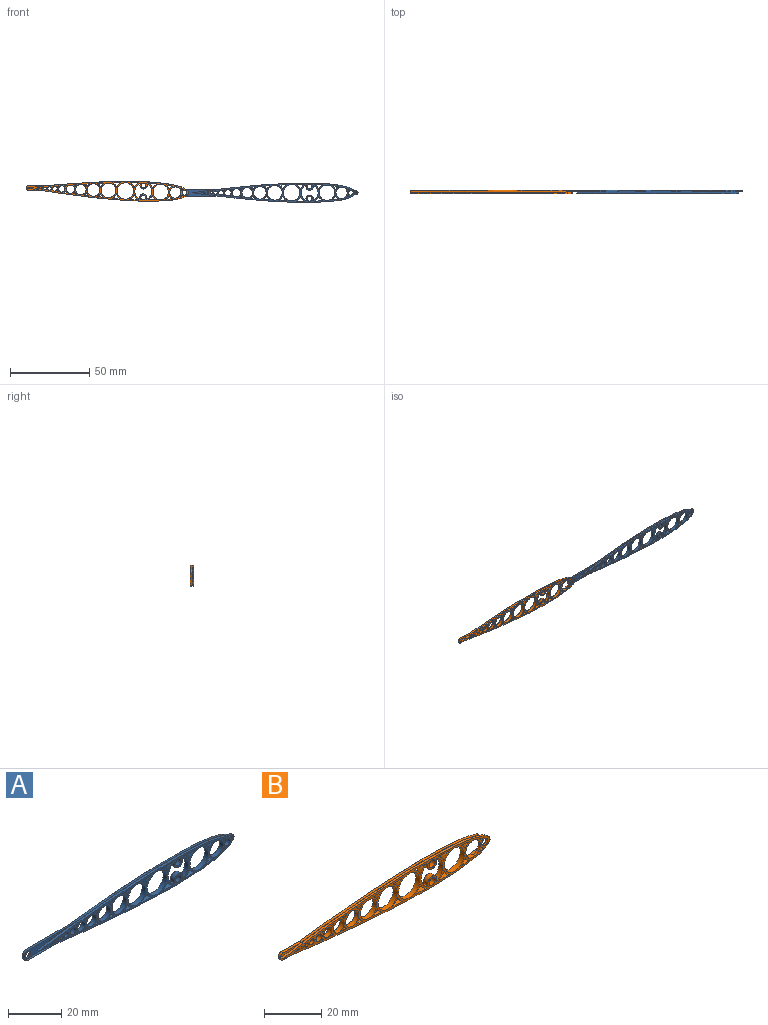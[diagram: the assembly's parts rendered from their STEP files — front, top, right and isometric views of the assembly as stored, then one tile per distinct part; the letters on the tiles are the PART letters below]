
ASSEMBLY  parts=2 mates=1
PART A: 123 faces, bbox 111.8x2x12.5 mm
  f0: extruded ~2.08x1.05mm, area 2.2mm2, adj f1,f111,f112,f114
  f1: extruded ~9.57x1.31mm, area 10.1mm2, adj f0,f2,f112,f114
  f2: extruded ~9.57x1.31mm, area 10.1mm2, adj f1,f3,f112,f114
  f3: extruded ~2.08x1.05mm, area 2.2mm2, adj f2,f4,f112,f114
  f4: extruded ~2.68x1.05mm, area 2.8mm2, adj f3,f5,f112,f114
  f5: extruded ~3.42x1.05mm, area 3.6mm2, adj f4,f6,f112,f114
  f6: extruded ~4.32x1.05mm, area 4.6mm2, adj f5,f7,f112,f114
  f7: extruded ~5.4x1.05mm, area 5.7mm2, adj f6,f8,f112,f114
  f8: extruded ~6.65x1.05mm, area 7mm2, adj f7,f9,f112,f114
  f9: extruded ~8.03x1.05mm, area 8.5mm2, adj f8,f10,f112,f114
  f10: extruded ~9.47x1.05mm, area 10mm2, adj f9,f11,f112,f114
  f11: extruded ~10.77x1.05mm, area 11.3mm2, adj f10,f12,f112,f114
  f12: extruded ~11.59x1.05mm, area 12.2mm2, adj f11,f13,f112,f114
  f13: extruded ~11.42x1.05mm, area 12mm2, adj f12,f14,f112,f114
  f14: extruded ~9.7x1.4mm, area 10.3mm2, adj f13,f15,f112,f114
  f15: extruded ~6.29x2.42mm, area 7.1mm2, adj f14,f16,f112,f114
  f16: extruded ~1.82x1.12mm, area 2.3mm2, adj f15,f17,f112,f114
  f17: extruded ~1.82x1.12mm, area 2.3mm2, adj f16,f18,f112,f114
  f18: extruded ~6.29x2.42mm, area 7.1mm2, adj f17,f19,f112,f114
  f19: extruded ~9.7x1.4mm, area 10.3mm2, adj f18,f20,f112,f114
  f20: extruded ~11.42x1.05mm, area 12mm2, adj f19,f21,f112,f114
  f21: extruded ~11.59x1.05mm, area 12.2mm2, adj f20,f22,f112,f114
  f22: extruded ~10.77x1.05mm, area 11.3mm2, adj f21,f23,f112,f114
  f23: extruded ~9.47x1.05mm, area 10mm2, adj f22,f24,f112,f114
  f24: extruded ~8.03x1.05mm, area 8.5mm2, adj f23,f25,f112,f114
  f25: extruded ~6.65x1.05mm, area 7mm2, adj f24,f26,f112,f114
  f26: extruded ~5.4x1.05mm, area 5.7mm2, adj f25,f27,f112,f114
  f27: extruded ~4.32x1.05mm, area 4.6mm2, adj f26,f28,f112,f114
  f28: extruded ~3.42x1.05mm, area 3.6mm2, adj f27,f111,f112,f114
  f29: extruded ~2x1.69mm, area 3.6mm2, adj f30,f75,f112,f113
  f30: cylinder r=4.35mm len=2mm, axis (0,1,0), area 3mm2, adj f29,f75,f112,f113
  f31: extruded ~2x1.69mm, area 3.6mm2, adj f32,f76,f112,f113
  f32: cylinder r=2.3mm len=2mm, axis (0,1,0), area 2.4mm2, adj f31,f76,f112,f113
  f33: extruded ~4.07x2mm, area 8.2mm2, adj f34,f77,f112,f113
  f34: cylinder r=4.35mm len=2.12mm, axis (0,1,0), area 6mm2, adj f33,f77,f112,f113
  f35: extruded ~4.07x2mm, area 8.2mm2, adj f36,f79,f112,f113
  f36: cylinder r=5.66mm len=2.61mm, axis (0,1,0), area 6.6mm2, adj f35,f79,f112,f113
  f37: extruded ~4.88x2mm, area 9.8mm2, adj f38,f80,f112,f113
  f38: cylinder r=5.98mm len=2.96mm, axis (0,1,0), area 7.8mm2, adj f37,f80,f112,f113
  f39: extruded ~4.88x2mm, area 9.8mm2, adj f40,f81,f112,f113
  f40: cylinder r=5.45mm len=2.72mm, axis (0,1,0), area 7.5mm2, adj f39,f81,f112,f113
  f41: extruded ~3.96x2mm, area 7.9mm2, adj f42,f82,f112,f113
  f42: cylinder r=5.45mm len=2.48mm, axis (0,1,0), area 6.4mm2, adj f41,f82,f112,f113
  f43: extruded ~3.96x2mm, area 7.9mm2, adj f44,f84,f112,f113
  f44: cylinder r=4.77mm len=2.19mm, axis (0,1,0), area 6.1mm2, adj f43,f84,f112,f113
  f45: extruded ~2.96x2mm, area 5.9mm2, adj f46,f86,f112,f113
  f46: cylinder r=4.07mm len=2mm, axis (0,1,0), area 4.5mm2, adj f45,f86,f112,f113
  f47: extruded ~2.96x2mm, area 5.9mm2, adj f48,f87,f112,f113
  f48: cylinder r=4.77mm len=2mm, axis (0,1,0), area 4.8mm2, adj f47,f87,f112,f113
  f49: extruded ~2.04x2mm, area 4.1mm2, adj f50,f88,f112,f113
  f50: cylinder r=4.07mm len=2mm, axis (0,1,0), area 3.4mm2, adj f49,f88,f112,f113
  f51: extruded ~2.04x2mm, area 4.1mm2, adj f52,f90,f112,f113
  f52: cylinder r=3.41mm len=2mm, axis (0,1,0), area 3.1mm2, adj f51,f90,f112,f113
  f53: extruded ~2x1.25mm, area 2.5mm2, adj f54,f92,f112,f113
  f54: cylinder r=2.83mm len=2mm, axis (0,1,0), area 1.9mm2, adj f53,f92,f112,f113
  f55: extruded ~2x1.25mm, area 2.5mm2, adj f56,f93,f112,f113
  f56: cylinder r=3.41mm len=2mm, axis (0,1,0), area 2.1mm2, adj f55,f93,f112,f113
  f57: cylinder r=5.34mm len=9.93mm, axis (0,1,0), area 25.5mm2, adj f58,f95,f112,f113
  f58: cylinder r=2.3mm len=4.6mm, axis (0,1,0), area 19.1mm2, adj f57,f59,f112,f113
  f59: cylinder r=5.34mm len=9.85mm, axis (0,1,0), area 25.1mm2, adj f58,f95,f112,f113
  f60: extruded ~5.47x2mm, area 10.9mm2, adj f61,f96,f112,f113
  f61: cylinder r=6.14mm len=3.18mm, axis (0,1,0), area 8.6mm2, adj f60,f96,f112,f113
  f62: extruded ~5.33x2mm, area 10.7mm2, adj f63,f98,f112,f113
  f63: cylinder r=5.66mm len=2.92mm, axis (0,1,0), area 8.1mm2, adj f62,f98,f112,f113
  f64: extruded ~5.33x2mm, area 10.7mm2, adj f65,f100,f112,f113
  f65: cylinder r=6.14mm len=3.15mm, axis (0,1,0), area 8.4mm2, adj f64,f100,f112,f113
  f66: extruded ~5.47x2mm, area 10.9mm2, adj f67,f102,f112,f113
  f67: cylinder r=5.98mm len=3.1mm, axis (0,1,0), area 8.5mm2, adj f66,f102,f112,f113
  f68: extruded ~2x0.61mm, area 1.2mm2, adj f69,f104,f112,f113
  f69: cylinder r=2.83mm len=2mm, axis (0,1,0), area 1mm2, adj f68,f104,f112,f113
  f70: extruded ~2x0.61mm, area 1.2mm2, adj f71,f106,f112,f113
  f71: cylinder r=2.33mm len=2mm, axis (0,1,0), area 1mm2, adj f70,f106,f112,f113
  f72: extruded ~2.71x2mm, area 5.5mm2, adj f73,f110,f112,f113
  f73: cylinder r=1.32mm len=2mm, axis (0,1,0), area 1.5mm2, adj f72,f110,f112,f113
  f74: cylinder r=1.5mm len=3mm, axis (0,1,0), area 18.8mm2, adj f112,f113
  f75: cylinder r=2.3mm len=2mm, axis (0,1,0), area 2.4mm2, adj f29,f30,f112,f113
  f76: cylinder r=4.35mm len=2mm, axis (0,1,0), area 3mm2, adj f31,f32,f112,f113
  f77: cylinder r=5.66mm len=2.61mm, axis (0,1,0), area 6.6mm2, adj f33,f34,f112,f113
  f78: cylinder r=3.55mm len=7.1mm, axis (0,1,0), area 44.6mm2, adj f112,f113
  f79: cylinder r=4.35mm len=2.12mm, axis (0,1,0), area 6mm2, adj f35,f36,f112,f113
  f80: cylinder r=5.45mm len=2.72mm, axis (0,1,0), area 7.5mm2, adj f37,f38,f112,f113
  f81: cylinder r=5.98mm len=2.96mm, axis (0,1,0), area 7.8mm2, adj f39,f40,f112,f113
  f82: cylinder r=4.77mm len=2.19mm, axis (0,1,0), area 6.1mm2, adj f41,f42,f112,f113
  f83: cylinder r=4.65mm len=9.3mm, axis (0,1,0), area 58.5mm2, adj f112,f113
  f84: cylinder r=5.45mm len=2.48mm, axis (0,1,0), area 6.4mm2, adj f43,f44,f112,f113
  f85: cylinder r=3.97mm len=7.94mm, axis (0,1,0), area 49.9mm2, adj f112,f113
  f86: cylinder r=4.77mm len=2mm, axis (0,1,0), area 4.8mm2, adj f45,f46,f112,f113
  f87: cylinder r=4.07mm len=2mm, axis (0,1,0), area 4.5mm2, adj f47,f48,f112,f113
  f88: cylinder r=3.41mm len=2mm, axis (0,1,0), area 3.1mm2, adj f49,f50,f112,f113
  f89: cylinder r=3.27mm len=6.54mm, axis (0,1,0), area 41.1mm2, adj f112,f113
  f90: cylinder r=4.07mm len=2mm, axis (0,1,0), area 3.4mm2, adj f51,f52,f112,f113
  f91: cylinder r=2.61mm len=5.22mm, axis (0,1,0), area 32.8mm2, adj f112,f113
  f92: cylinder r=3.41mm len=2mm, axis (0,1,0), area 2.1mm2, adj f53,f54,f112,f113
  f93: cylinder r=2.83mm len=2mm, axis (0,1,0), area 1.9mm2, adj f55,f56,f112,f113
  f94: cylinder r=5.18mm len=10.36mm, axis (0,1,0), area 65.1mm2, adj f112,f113
  f95: cylinder r=2.3mm len=4.6mm, axis (0,1,0), area 19.1mm2, adj f57,f59,f112,f113
  f96: cylinder r=5.98mm len=3.1mm, axis (0,1,0), area 8.5mm2, adj f60,f61,f112,f113
  f97: cylinder r=1.5mm len=3mm, axis (0,1,0), area 18.8mm2, adj f112,f113
  f98: cylinder r=6.14mm len=3.15mm, axis (0,1,0), area 8.4mm2, adj f62,f63,f112,f113
  f99: cylinder r=4.86mm len=9.72mm, axis (0,1,0), area 61.1mm2, adj f112,f113
  f100: cylinder r=5.66mm len=2.92mm, axis (0,1,0), area 8.1mm2, adj f64,f65,f112,f113
  f101: cylinder r=1.5mm len=3mm, axis (0,1,0), area 18.8mm2, adj f112,f113
  f102: cylinder r=6.14mm len=3.18mm, axis (0,1,0), area 8.6mm2, adj f66,f67,f112,f113
  f103: cylinder r=1.5mm len=3mm, axis (0,1,0), area 18.8mm2, adj f112,f113
  f104: cylinder r=2.33mm len=2mm, axis (0,1,0), area 1mm2, adj f68,f69,f112,f113
  f105: cylinder r=2.03mm len=4.06mm, axis (0,1,0), area 25.5mm2, adj f112,f113
  f106: cylinder r=2.83mm len=2mm, axis (0,1,0), area 1mm2, adj f70,f71,f112,f113
  f107: cylinder r=1.12mm len=2.25mm, axis (0,1,0), area 14.1mm2, adj f112,f113
  f108: cylinder r=0.79mm len=2mm, axis (0,1,0), area 9.9mm2, adj f112,f113
  f109: cylinder r=0.52mm len=2mm, axis (0,1,0), area 6.6mm2, adj f112,f113
  f110: extruded ~2.71x2mm, area 5.5mm2, adj f72,f73,f112,f113
  f111: extruded ~2.68x1.05mm, area 2.8mm2, adj f0,f28,f112,f114
  f112: plane 102.5x12.3mm, normal (0,-1,0), area 317.3mm2, adj f0,f1,f2,f3,f4,f5,f6,f7
  f113: plane 111.8x12.5mm, normal (0,1,0), area 401.7mm2, adj f29,f30,f31,f32,f33,f34,f35,f36
  f114: plane 111.8x12.5mm, normal (0,-1,0), area 84.4mm2, adj f0,f1,f2,f3,f4,f5,f6,f7
  f115: cylinder r=2.3mm len=4.6mm, axis (0,1,0), area 6.9mm2, adj f113,f114,f116,f121
  f116: plane 21.74x0.95mm, normal (0,0,-1), area 20.6mm2, adj f113,f114,f115,f117
  f117: extruded ~85.5x5.15mm, area 82.2mm2, adj f113,f114,f116,f118
  f118: cylinder r=1.4mm len=2.8mm, axis (0,1,0), area 6mm2, adj f113,f114,f117,f119
  f119: extruded ~85.5x5.15mm, area 82.2mm2, adj f113,f114,f118,f121
  f120: cylinder r=0.6mm len=1.2mm, axis (0,1,0), area 3.6mm2, adj f113,f114
  f121: plane 21.74x0.95mm, normal (0,0,1), area 20.6mm2, adj f113,f114,f115,f119
  f122: cylinder r=1.5mm len=3mm, axis (0,1,0), area 9mm2, adj f113,f114
PART B: 131 faces, bbox 102.7x2x12.5 mm
  f0: cylinder r=3.55mm len=7.1mm, axis (0,1,0), area 34.6mm2, adj f1,f120,f126,f127,f128
  f1: plane 98.43x12.5mm, normal (0,1,0), area 333.6mm2, adj f0,f36,f42,f43,f44,f45,f46,f47
  f2: plane 98.35x12.5mm, normal (0,-1,0), area 33.5mm2, adj f3,f4,f5,f6,f7,f8,f9,f10
  f3: extruded ~6.86x0.95mm, area 6.6mm2, adj f2,f4,f119,f120
  f4: extruded ~2.71x0.95mm, area 2.6mm2, adj f2,f3,f5,f120
  f5: extruded ~2.71x0.95mm, area 2.6mm2, adj f2,f4,f6,f120
  f6: extruded ~6.86x0.95mm, area 6.6mm2, adj f2,f5,f7,f120
  f7: extruded ~2.08x0.95mm, area 2mm2, adj f2,f6,f8,f120
  f8: extruded ~2.68x0.95mm, area 2.6mm2, adj f2,f7,f9,f120
  f9: extruded ~3.42x0.95mm, area 3.3mm2, adj f2,f8,f10,f120
  f10: extruded ~4.32x0.95mm, area 4.1mm2, adj f2,f9,f11,f120
  f11: extruded ~5.4x0.95mm, area 5.2mm2, adj f2,f10,f12,f120
  f12: extruded ~6.65x0.95mm, area 6.3mm2, adj f2,f11,f13,f120
  f13: extruded ~8.03x0.95mm, area 7.7mm2, adj f2,f12,f14,f120
  f14: extruded ~9.47x0.95mm, area 9mm2, adj f2,f13,f15,f120
  f15: extruded ~10.77x0.95mm, area 10.2mm2, adj f2,f14,f16,f120
  f16: extruded ~11.59x0.95mm, area 11mm2, adj f2,f15,f17,f120
  f17: extruded ~11.42x0.95mm, area 10.9mm2, adj f2,f16,f18,f120
  f18: extruded ~9.7x1.4mm, area 9.3mm2, adj f2,f17,f19,f120
  f19: extruded ~3.02x0.95mm, area 3mm2, adj f2,f18,f20,f120
  f20: extruded ~3.27x1.59mm, area 3.5mm2, adj f19,f21,f120,f126
  f21: extruded ~1.82x1.12mm, area 2.1mm2, adj f20,f22,f120,f126
  f22: extruded ~1.82x1.12mm, area 2.1mm2, adj f21,f23,f120,f126
  f23: extruded ~3.27x1.59mm, area 3.5mm2, adj f22,f24,f120,f126
  f24: extruded ~3.02x0.95mm, area 3mm2, adj f2,f23,f25,f120
  f25: extruded ~9.7x1.4mm, area 9.3mm2, adj f2,f24,f26,f120
  f26: extruded ~11.42x0.95mm, area 10.9mm2, adj f2,f25,f27,f120
  f27: extruded ~11.59x0.95mm, area 11mm2, adj f2,f26,f28,f120
  f28: extruded ~10.77x0.95mm, area 10.2mm2, adj f2,f27,f29,f120
  f29: extruded ~9.47x0.95mm, area 9mm2, adj f2,f28,f30,f120
  f30: extruded ~8.03x0.95mm, area 7.7mm2, adj f2,f29,f31,f120
  f31: extruded ~6.65x0.95mm, area 6.3mm2, adj f2,f30,f32,f120
  f32: extruded ~5.4x0.95mm, area 5.2mm2, adj f2,f31,f33,f120
  f33: extruded ~4.32x0.95mm, area 4.1mm2, adj f2,f32,f34,f120
  f34: extruded ~3.42x0.95mm, area 3.3mm2, adj f2,f33,f35,f120
  f35: extruded ~2.68x0.95mm, area 2.6mm2, adj f2,f34,f119,f120
  f36: extruded ~2x0.12mm, area 0.3mm2, adj f1,f37,f84,f120,f128,f129
  f37: cylinder r=4.35mm len=1.29mm, axis (0,1,0), area 1.4mm2, adj f36,f38,f120,f126
  f38: cylinder r=2.3mm len=0.95mm, axis (0,1,0), area 1.1mm2, adj f37,f84,f120,f126
  f39: extruded ~1.57x0.95mm, area 1.6mm2, adj f40,f85,f120,f126
  f40: cylinder r=2.3mm len=0.95mm, axis (0,1,0), area 1.1mm2, adj f39,f41,f120,f126
  f41: cylinder r=4.35mm len=1.29mm, axis (0,1,0), area 1.4mm2, adj f40,f85,f120,f126
  f42: extruded ~4.07x2mm, area 8.2mm2, adj f1,f43,f86,f120
  f43: cylinder r=4.35mm len=2.12mm, axis (0,1,0), area 6mm2, adj f1,f42,f86,f120
  f44: extruded ~4.07x2mm, area 8.2mm2, adj f1,f45,f87,f120
  f45: cylinder r=5.66mm len=2.61mm, axis (0,1,0), area 6.6mm2, adj f1,f44,f87,f120
  f46: extruded ~4.88x2mm, area 9.8mm2, adj f1,f47,f88,f120
  f47: cylinder r=5.98mm len=2.96mm, axis (0,1,0), area 7.8mm2, adj f1,f46,f88,f120
  f48: extruded ~4.88x2mm, area 9.8mm2, adj f1,f49,f89,f120
  f49: cylinder r=5.45mm len=2.72mm, axis (0,1,0), area 7.5mm2, adj f1,f48,f89,f120
  f50: extruded ~3.96x2mm, area 7.9mm2, adj f1,f51,f90,f120
  f51: cylinder r=5.45mm len=2.48mm, axis (0,1,0), area 6.4mm2, adj f1,f50,f90,f120
  f52: extruded ~3.96x2mm, area 7.9mm2, adj f1,f53,f92,f120
  f53: cylinder r=4.77mm len=2.19mm, axis (0,1,0), area 6.1mm2, adj f1,f52,f92,f120
  f54: extruded ~2.96x2mm, area 5.9mm2, adj f1,f55,f94,f120
  f55: cylinder r=4.07mm len=2mm, axis (0,1,0), area 4.5mm2, adj f1,f54,f94,f120
  f56: extruded ~2.96x2mm, area 5.9mm2, adj f1,f57,f95,f120
  f57: cylinder r=4.77mm len=2mm, axis (0,1,0), area 4.8mm2, adj f1,f56,f95,f120
  f58: extruded ~2.04x2mm, area 4.1mm2, adj f1,f59,f96,f120
  f59: cylinder r=4.07mm len=2mm, axis (0,1,0), area 3.4mm2, adj f1,f58,f96,f120
  f60: extruded ~2.04x2mm, area 4.1mm2, adj f1,f61,f98,f120
  f61: cylinder r=3.41mm len=2mm, axis (0,1,0), area 3.1mm2, adj f1,f60,f98,f120
  f62: extruded ~2x1.25mm, area 2.5mm2, adj f1,f63,f100,f120
  f63: cylinder r=2.83mm len=2mm, axis (0,1,0), area 1.9mm2, adj f1,f62,f100,f120
  f64: extruded ~2x1.25mm, area 2.5mm2, adj f1,f65,f101,f120
  f65: cylinder r=3.41mm len=2mm, axis (0,1,0), area 2.1mm2, adj f1,f64,f101,f120
  f66: cylinder r=5.34mm len=9.93mm, axis (0,1,0), area 25.5mm2, adj f1,f67,f103,f120
  f67: cylinder r=2.3mm len=4.6mm, axis (0,1,0), area 19.1mm2, adj f1,f66,f68,f120
  f68: cylinder r=5.34mm len=9.85mm, axis (0,1,0), area 25.1mm2, adj f1,f67,f103,f120
  f69: extruded ~5.47x2mm, area 10.9mm2, adj f1,f70,f104,f120
  f70: cylinder r=6.14mm len=3.18mm, axis (0,1,0), area 8.6mm2, adj f1,f69,f104,f120
  f71: extruded ~5.33x2mm, area 10.7mm2, adj f1,f72,f106,f120
  f72: cylinder r=5.66mm len=2.92mm, axis (0,1,0), area 8.1mm2, adj f1,f71,f106,f120
  f73: extruded ~5.33x2mm, area 10.7mm2, adj f1,f74,f108,f120
  f74: cylinder r=6.14mm len=3.15mm, axis (0,1,0), area 8.4mm2, adj f1,f73,f108,f120
  f75: extruded ~5.47x2mm, area 10.9mm2, adj f1,f76,f110,f120
  f76: cylinder r=5.98mm len=3.1mm, axis (0,1,0), area 8.5mm2, adj f1,f75,f110,f120
  f77: extruded ~2x0.61mm, area 1.2mm2, adj f1,f78,f112,f120
  f78: cylinder r=2.83mm len=2mm, axis (0,1,0), area 1mm2, adj f1,f77,f112,f120
  f79: extruded ~2x0.61mm, area 1.2mm2, adj f1,f80,f114,f120
  f80: cylinder r=2.33mm len=2mm, axis (0,1,0), area 1mm2, adj f1,f79,f114,f120
  f81: extruded ~2.71x2mm, area 5.5mm2, adj f1,f82,f118,f120
  f82: cylinder r=1.32mm len=2mm, axis (0,1,0), area 1.5mm2, adj f1,f81,f118,f120
  f83: cylinder r=1.5mm len=3mm, axis (0,1,0), area 9mm2, adj f120,f126
  f84: extruded ~1.57x0.95mm, area 1.6mm2, adj f36,f38,f120,f126
  f85: extruded ~2x0.12mm, area 0.3mm2, adj f1,f39,f41,f120,f127,f130
  f86: cylinder r=5.66mm len=2.61mm, axis (0,1,0), area 6.6mm2, adj f1,f42,f43,f120
  f87: cylinder r=4.35mm len=2.12mm, axis (0,1,0), area 6mm2, adj f1,f44,f45,f120
  f88: cylinder r=5.45mm len=2.72mm, axis (0,1,0), area 7.5mm2, adj f1,f46,f47,f120
  f89: cylinder r=5.98mm len=2.96mm, axis (0,1,0), area 7.8mm2, adj f1,f48,f49,f120
  f90: cylinder r=4.77mm len=2.19mm, axis (0,1,0), area 6.1mm2, adj f1,f50,f51,f120
  f91: cylinder r=4.65mm len=9.3mm, axis (0,1,0), area 58.5mm2, adj f1,f120
  f92: cylinder r=5.45mm len=2.48mm, axis (0,1,0), area 6.4mm2, adj f1,f52,f53,f120
  f93: cylinder r=3.97mm len=7.94mm, axis (0,1,0), area 49.9mm2, adj f1,f120
  f94: cylinder r=4.77mm len=2mm, axis (0,1,0), area 4.8mm2, adj f1,f54,f55,f120
  f95: cylinder r=4.07mm len=2mm, axis (0,1,0), area 4.5mm2, adj f1,f56,f57,f120
  f96: cylinder r=3.41mm len=2mm, axis (0,1,0), area 3.1mm2, adj f1,f58,f59,f120
  f97: cylinder r=3.27mm len=6.54mm, axis (0,1,0), area 41.1mm2, adj f1,f120
  f98: cylinder r=4.07mm len=2mm, axis (0,1,0), area 3.4mm2, adj f1,f60,f61,f120
  f99: cylinder r=2.61mm len=5.22mm, axis (0,1,0), area 32.8mm2, adj f1,f120
  f100: cylinder r=3.41mm len=2mm, axis (0,1,0), area 2.1mm2, adj f1,f62,f63,f120
  f101: cylinder r=2.83mm len=2mm, axis (0,1,0), area 1.9mm2, adj f1,f64,f65,f120
  f102: cylinder r=5.18mm len=10.36mm, axis (0,1,0), area 65.1mm2, adj f1,f120
  f103: cylinder r=2.3mm len=4.6mm, axis (0,1,0), area 19.1mm2, adj f1,f66,f68,f120
  f104: cylinder r=5.98mm len=3.1mm, axis (0,1,0), area 8.5mm2, adj f1,f69,f70,f120
  f105: cylinder r=1.5mm len=3mm, axis (0,1,0), area 18.8mm2, adj f1,f120
  f106: cylinder r=6.14mm len=3.15mm, axis (0,1,0), area 8.4mm2, adj f1,f71,f72,f120
  f107: cylinder r=4.86mm len=9.72mm, axis (0,1,0), area 61.1mm2, adj f1,f120
  f108: cylinder r=5.66mm len=2.92mm, axis (0,1,0), area 8.1mm2, adj f1,f73,f74,f120
  f109: cylinder r=1.5mm len=3mm, axis (0,1,0), area 18.8mm2, adj f1,f120
  f110: cylinder r=6.14mm len=3.18mm, axis (0,1,0), area 8.6mm2, adj f1,f75,f76,f120
  f111: cylinder r=1.5mm len=3mm, axis (0,1,0), area 18.8mm2, adj f1,f120
  f112: cylinder r=2.33mm len=2mm, axis (0,1,0), area 1mm2, adj f1,f77,f78,f120
  f113: cylinder r=2.03mm len=4.06mm, axis (0,1,0), area 25.5mm2, adj f1,f120
  f114: cylinder r=2.83mm len=2mm, axis (0,1,0), area 1mm2, adj f1,f79,f80,f120
  f115: cylinder r=1.12mm len=2.25mm, axis (0,1,0), area 14.1mm2, adj f1,f120
  f116: cylinder r=0.79mm len=2mm, axis (0,1,0), area 9.9mm2, adj f1,f120
  f117: cylinder r=0.52mm len=2mm, axis (0,1,0), area 6.6mm2, adj f1,f120
  f118: extruded ~2.71x2mm, area 5.5mm2, adj f1,f81,f82,f120
  f119: extruded ~2.08x0.95mm, area 2mm2, adj f2,f3,f35,f120
  f120: plane 102.5x12.3mm, normal (0,-1,0), area 317.3mm2, adj f0,f3,f4,f5,f6,f7,f8,f9
  f121: plane 8.99x1.05mm, normal (0,0,1), area 9.4mm2, adj f1,f2,f122,f125
  f122: cylinder r=1.5mm len=3mm, axis (0,1,0), area 4.9mm2, adj f1,f2,f121,f123
  f123: plane 8.99x1.05mm, normal (0,0,-1), area 9.4mm2, adj f1,f2,f122,f124
  f124: extruded ~87.62x4.75mm, area 92.4mm2, adj f1,f2,f123,f129
  f125: extruded ~87.62x4.75mm, area 92.4mm2, adj f1,f2,f121,f130
  f126: plane 7.59x6.93mm, normal (0,1,0), area 17.2mm2, adj f0,f20,f21,f22,f23,f37,f38,f39
  f127: extruded ~2.56x1.05mm, area 2.8mm2, adj f0,f1,f85,f126
  f128: extruded ~2.56x1.05mm, area 2.8mm2, adj f0,f1,f36,f126
  f129: cylinder r=0.45mm len=1.05mm, axis (0,1,0), area 1.5mm2, adj f1,f2,f36,f124,f126
  f130: cylinder r=0.45mm len=1.05mm, axis (0,1,0), area 1.5mm2, adj f1,f2,f85,f125,f126
PLACE A t=(-11.34,90.52,0)mm
PLACE B rot(axis=(0,1,0),1.8deg) t=(-116.29,90.58,1.52)mm
MATE revolute A.f122 <-> B.f83  axis (0,-1,0) through (-67.59,89.58,0)mm
